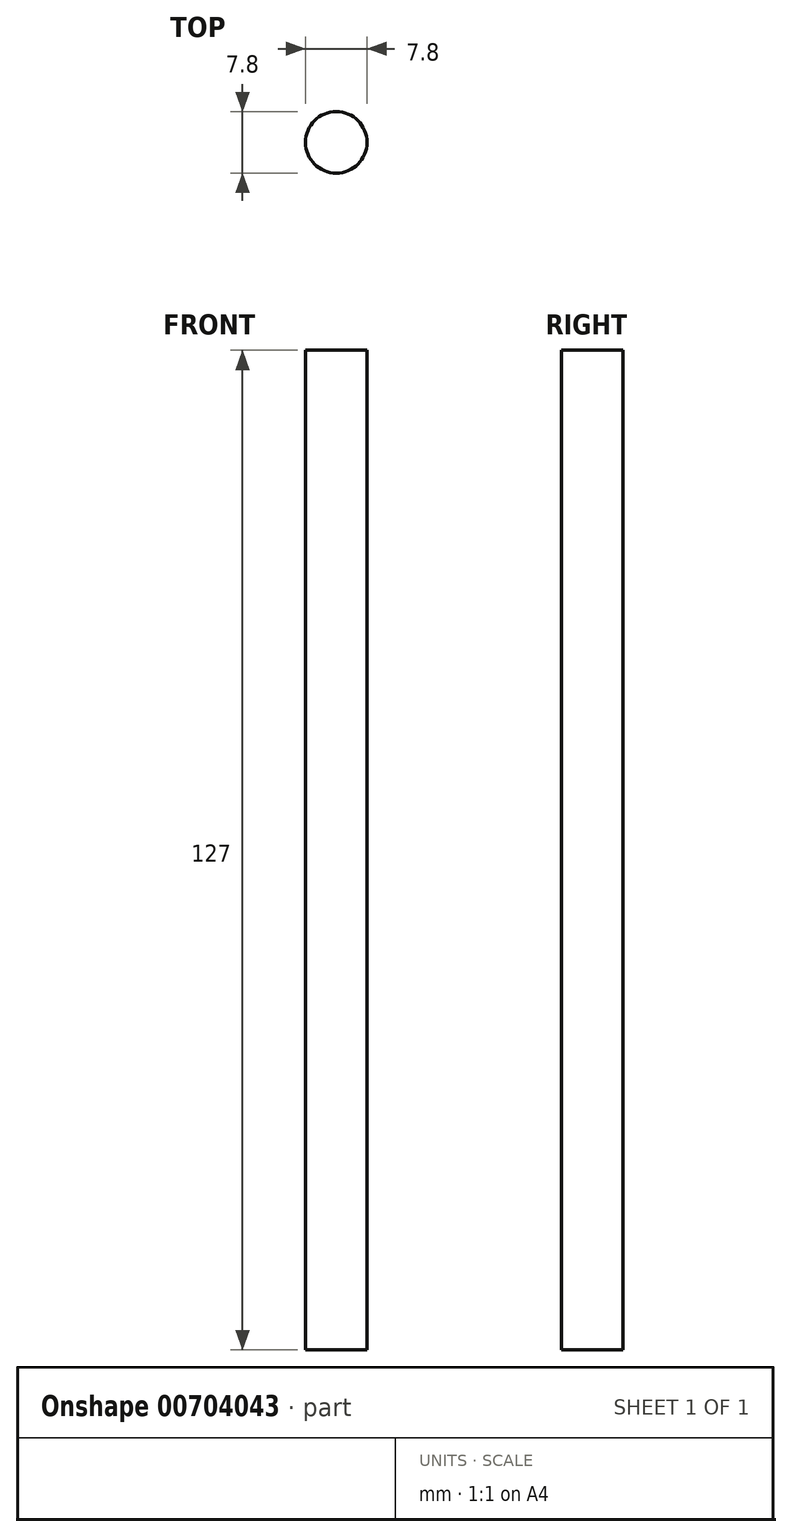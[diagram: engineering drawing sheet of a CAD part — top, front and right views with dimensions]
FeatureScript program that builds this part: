
annotation { "Feature Type Name" : "Feature", "Feature Type Description" : "" }
export const myFeature = defineFeature(function(context is Context, id is Id, definition is map)
    precondition{}
    {
        {
            var Q0;
            Q0=qCreatedBy(makeId("Top.planeOp"),FACE);
            var sketch = newSketch(context, id + "F0", { "sketchPlane" : qUnion([Q0])});
            skCircle(sketch, "E0", {"center": v(0, 0) * mm, "radius": 3.9 * mm});
            skSolve(sketch);
        }
        {
            var Q0;
            Q0=makeQuery(id+"F0.imprint","IMPRINT",FACE,{"disambiguationData":[TD([[makeQuery(id+"F0.imprint","IMPRINT",EDGE,{"derivedFrom":sQuery(id+"F0.wireOp",EDGE,"E0")}),1.0]])]});
            extrude(context, id + "F1", {"entities" : qUnion([Q0]), "depth" : 127 * mm, "offsetDistance" : 25.4 * mm});
        }
    });
